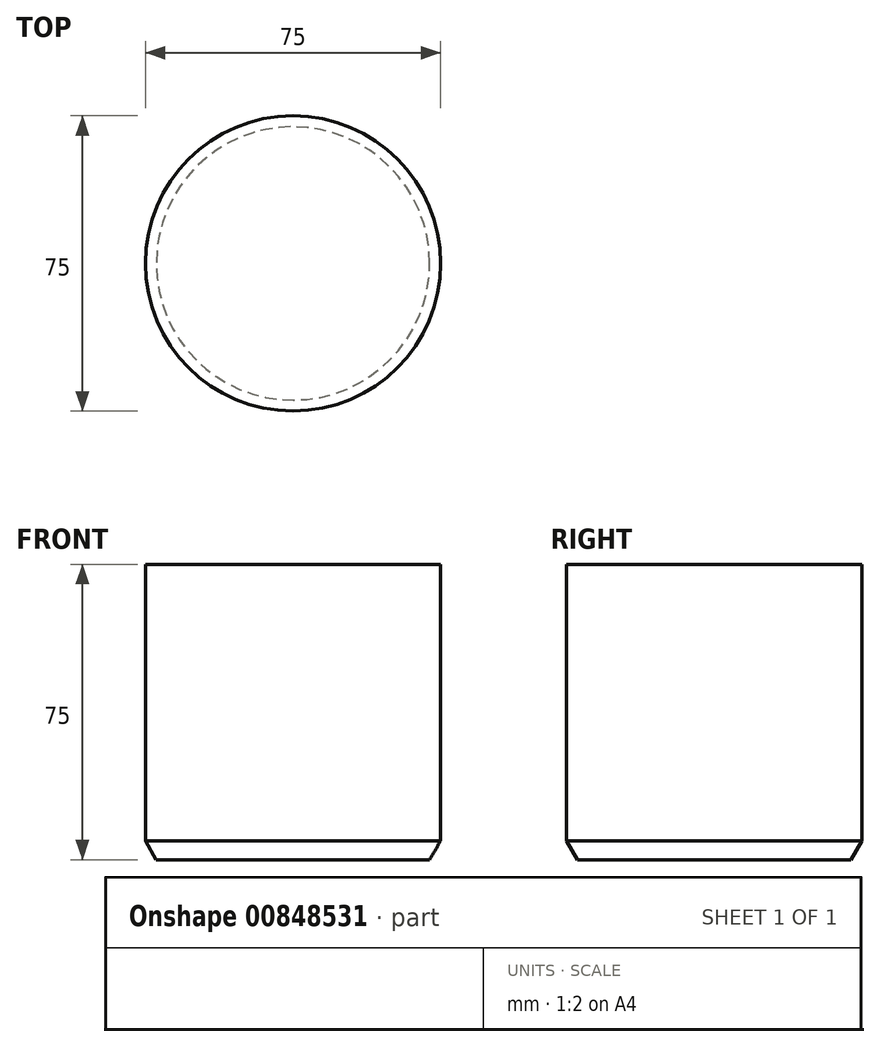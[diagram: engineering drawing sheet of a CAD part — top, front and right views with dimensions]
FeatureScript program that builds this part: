
annotation { "Feature Type Name" : "Feature", "Feature Type Description" : "" }
export const myFeature = defineFeature(function(context is Context, id is Id, definition is map)
    precondition{}
    {
        {
            var Q0;
            Q0=qCreatedBy(makeId("Top.planeOp"),FACE);
            var sketch = newSketch(context, id + "F0", { "sketchPlane" : qUnion([Q0])});
            skCircle(sketch, "E0", {"center": v(0, 0) * mm, "radius": 37.5 * mm});
            skSolve(sketch);
        }
        {
            var Q0;
            Q0=makeQuery(id+"F0.imprint","IMPRINT",FACE,{"disambiguationData":[TD([[makeQuery(id+"F0.imprint","IMPRINT",EDGE,{"derivedFrom":sQuery(id+"F0.wireOp",EDGE,"E0")}),1.0]])]});
            extrude(context, id + "F1", {"entities" : qUnion([Q0]), "depth" : 75 * mm, "offsetDistance" : 25 * mm});
        }
        {
            var Q0;
            Q0=makeQuery(id+"F1.opExtrude","CAP_EDGE",EDGE,{"disambiguationData":[OSD([sQuery(id+"F0.wireOp",EDGE,"E0")])],"isStart":true});
            chamfer(context, id + "F2", {"entities" : qUnion([Q0]), "chamferType" : ChamferType.OFFSET_ANGLE, "width" : 4.8 * mm, "oppositeDirection" : false, "angle" : 30 * degree, "tangentPropagation" : true});
        }
    });
